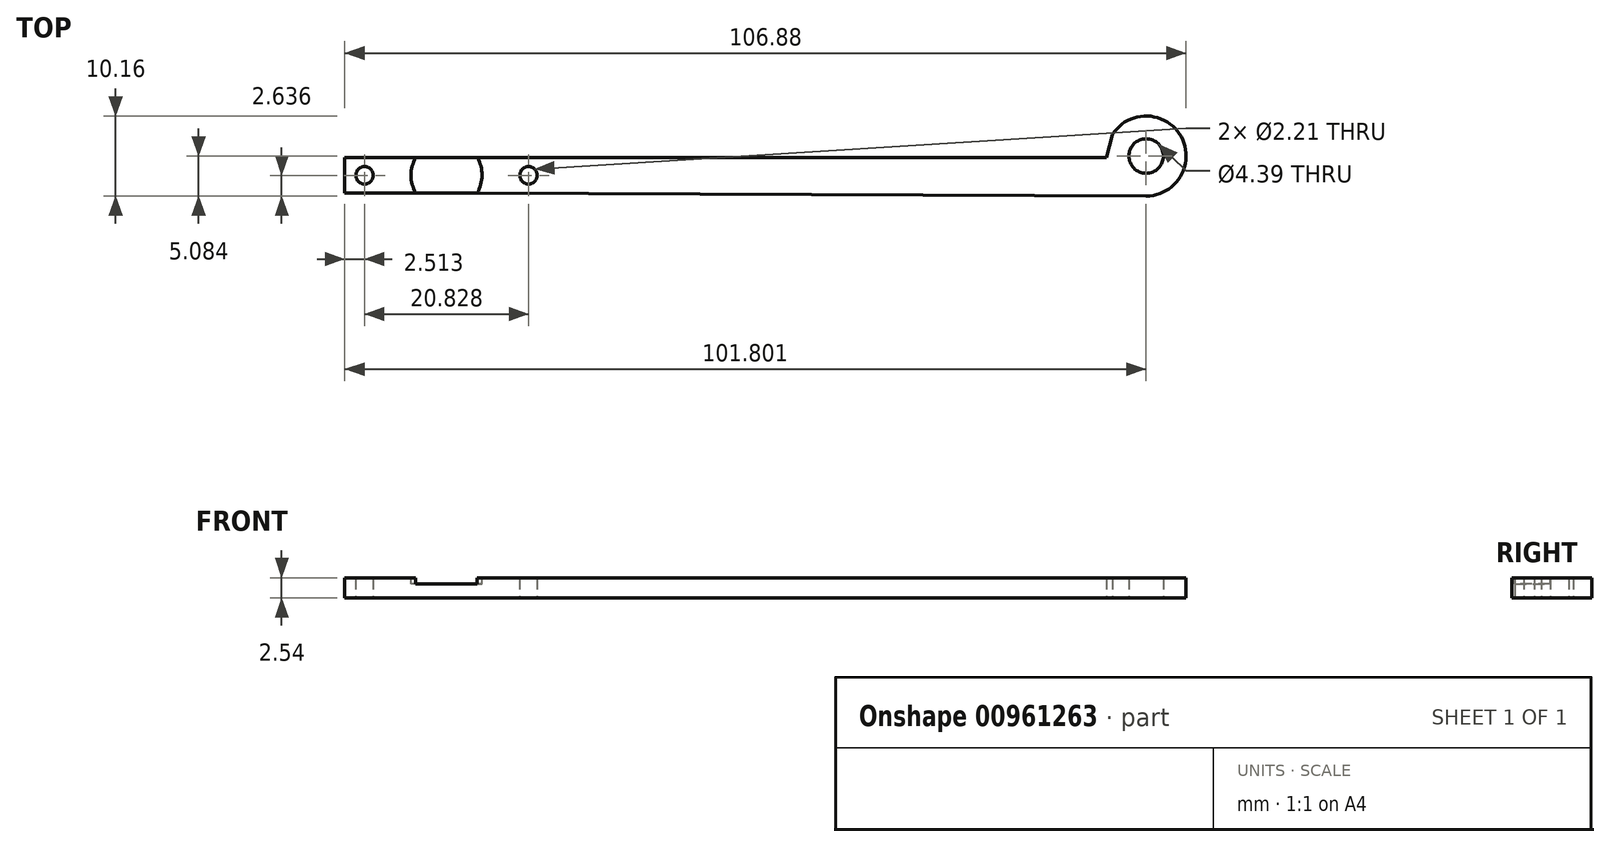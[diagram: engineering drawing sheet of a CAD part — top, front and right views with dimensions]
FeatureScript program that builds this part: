
annotation { "Feature Type Name" : "Feature", "Feature Type Description" : "" }
export const myFeature = defineFeature(function(context is Context, id is Id, definition is map)
    precondition{}
    {
        {
            var Q0;
            Q0=qCreatedBy(makeId("Top.planeOp"),FACE);
            var sketch = newSketch(context, id + "F0", { "sketchPlane" : qUnion([Q0])});
            skLineSegment(sketch, "E0", {"start": v(-4.9, 9.71) * mm, "end": v(74.35, 9.71) * mm});
            skLineSegment(sketch, "E1", {"start": v(83.98, 4.83) * mm, "end": v(-4.9, 5.22) * mm});
            skArc(sketch, "E2", {"start": v(83.98, 4.83) * mm, "mid": v(88.44, 12.36) * mm, "end": v(79.7, 12.65) * mm});
            skCircle(sketch, "E3", {"center": v(83.98, 9.91) * mm, "radius": 2.2 * mm});
            skCircle(sketch, "E4", {"center": v(5.52, 7.47) * mm, "radius": 1.1 * mm});
            skLineSegment(sketch, "E5", {"start": v(-4.9, 7.47) * mm, "end": v(24.29, 7.47) * mm, "construction": true});
            skLineSegment(sketch, "E6", {"start": v(-4.9, 9.71) * mm, "end": v(-15.33, 9.71) * mm});
            skLineSegment(sketch, "E7", {"start": v(-17.82, 7.76) * mm, "end": v(-17.82, 6.92) * mm});
            skLineSegment(sketch, "E8", {"start": v(-15.28, 5.22) * mm, "end": v(-4.9, 5.22) * mm});
            skLineSegment(sketch, "E9", {"start": v(-4.9, 9.71) * mm, "end": v(-4.9, 5.22) * mm, "construction": true});
            skCircle(sketch, "E10.MirrorC", {"center": v(-15.3, 7.47) * mm, "radius": 1.1 * mm});
            skPoint(sketch, "E11.visualSharp", {"position": v(-17.82, 9.71) * mm});
            skPoint(sketch, "E12.visualSharp", {"position": v(-17.82, 5.22) * mm});
            skPoint(sketch, "E13.visualSharp", {"position": v(78.9, 9.71) * mm});
            skLineSegment(sketch, "E14", {"start": v(74.35, 9.71) * mm, "end": v(78.9, 9.71) * mm});
            skLineSegment(sketch, "E15", {"start": v(79.7, 12.65) * mm, "end": v(78.9, 9.71) * mm});
            skLineSegment(sketch, "E16", {"start": v(-15.33, 9.71) * mm, "end": v(-17.82, 9.71) * mm});
            skLineSegment(sketch, "E17", {"start": v(-17.82, 9.71) * mm, "end": v(-17.82, 7.76) * mm});
            skLineSegment(sketch, "E18", {"start": v(-17.82, 6.92) * mm, "end": v(-17.82, 5.22) * mm});
            skLineSegment(sketch, "E19", {"start": v(-17.82, 5.22) * mm, "end": v(-15.28, 5.22) * mm});
            skSolve(sketch);
        }
        {
            var Q0;
            Q0=makeQuery(id+"F0.imprint","IMPRINT",FACE,{"disambiguationData":[TD([[makeQuery(id+"F0.imprint","IMPRINT",EDGE,{"derivedFrom":sQuery(id+"F0.wireOp",EDGE,"E0")}),-1.0]])]});
            extrude(context, id + "F1", {"entities" : qUnion([Q0]), "depth" : 2.54 * mm, "offsetDistance" : 25.4 * mm});
        }
        {
            var Q0;
            Q0=makeQuery(id+"F1.opExtrude","CAP_FACE",FACE,{"disambiguationData":[OSD([sQuery(id+"F0.wireOp",EDGE,"E0"),sQuery(id+"F0.wireOp",EDGE,"E1"),sQuery(id+"F0.wireOp",EDGE,"E2"),sQuery(id+"F0.wireOp",EDGE,"E3"),sQuery(id+"F0.wireOp",EDGE,"E4"),sQuery(id+"F0.wireOp",EDGE,"E6"),sQuery(id+"F0.wireOp",EDGE,"E7"),sQuery(id+"F0.wireOp",EDGE,"E8"),sQuery(id+"F0.wireOp",EDGE,"E10.MirrorC"),sQuery(id+"F0.wireOp",EDGE,"E14"),sQuery(id+"F0.wireOp",EDGE,"E15"),sQuery(id+"F0.wireOp",EDGE,"E16"),sQuery(id+"F0.wireOp",EDGE,"E17"),sQuery(id+"F0.wireOp",EDGE,"E18"),sQuery(id+"F0.wireOp",EDGE,"E19")])],"isStart":false});
            var sketch = newSketch(context, id + "F2", { "sketchPlane" : qUnion([Q0])});
            skLineSegment(sketch, "E20", {"start": v(-4.9, 5.22) * mm, "end": v(-4.9, 9.71) * mm, "construction": true});
            skCircle(sketch, "E21", {"center": v(-4.9, 7.47) * mm, "radius": 4.5 * mm});
            skSolve(sketch);
        }
        {
            var Q0;
            {var subQ1=makeQuery(id+"F1.opExtrude","CAP_EDGE",EDGE,{"disambiguationData":[OSD([sQuery(id+"F0.wireOp",EDGE,"E1")])],"isStart":false});var subQ3=sQuery(id+"F2.wireOp",EDGE,"E21");var subQ4=makeQuery(id+"F2.imprint","INTERSECT",VERTEX,{"derivedFrom":[subQ1,subQ3]});Q0=makeQuery(id+"F2.imprint","IMPRINT",FACE,{"disambiguationData":[TD([[makeQuery(id+"F2.imprint","IMPRINT",EDGE,{"disambiguationData":[TD([[subQ4,-1.0]])],"derivedFrom":subQ1}),-1.0]])]});}
            extrude(context, id + "F3", {"entities" : qUnion([Q0]), "operationType" : NewBodyOperationType.REMOVE, "oppositeDirection" : true, "depth" : 0.76 * mm, "offsetDistance" : 25.4 * mm});
        }
    });
